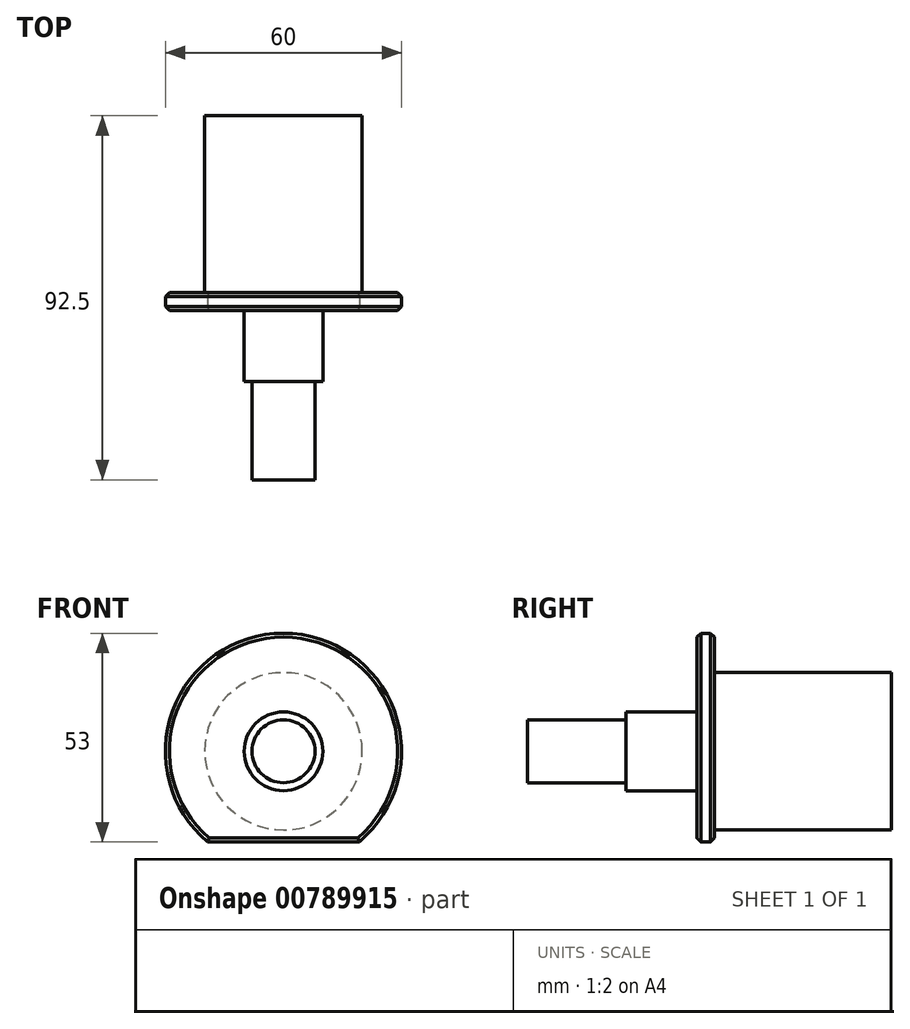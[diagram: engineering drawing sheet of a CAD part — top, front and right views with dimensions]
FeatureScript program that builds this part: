
annotation { "Feature Type Name" : "Feature", "Feature Type Description" : "" }
export const myFeature = defineFeature(function(context is Context, id is Id, definition is map)
    precondition{}
    {
        {
            var Q0;
            Q0=qCreatedBy(makeId("Right.planeOp"),FACE);
            var sketch = newSketch(context, id + "F0", { "sketchPlane" : qUnion([Q0])});
            skLineSegment(sketch, "E0", {"start": v(0, 0) * mm, "end": v(0, -8) * mm});
            skLineSegment(sketch, "E1", {"start": v(0, -8) * mm, "end": v(25, -8) * mm});
            skLineSegment(sketch, "E2", {"start": v(25, -8) * mm, "end": v(25, -10) * mm});
            skLineSegment(sketch, "E3", {"start": v(25, -10) * mm, "end": v(43, -10) * mm});
            skLineSegment(sketch, "E4", {"start": v(43, -10) * mm, "end": v(43, -30) * mm});
            skLineSegment(sketch, "E5", {"start": v(43, -30) * mm, "end": v(47.5, -30) * mm});
            skLineSegment(sketch, "E6", {"start": v(47.5, -30) * mm, "end": v(47.5, -20) * mm});
            skLineSegment(sketch, "E7", {"start": v(47.5, -20) * mm, "end": v(92.5, -20) * mm});
            skLineSegment(sketch, "E8", {"start": v(92.5, -20) * mm, "end": v(92.5, 0) * mm});
            skLineSegment(sketch, "E9", {"start": v(92.5, 0) * mm, "end": v(0, 0) * mm});
            skLineSegment(sketch, "E10", {"start": v(-68.98, 0) * mm, "end": v(144.58, 0) * mm, "construction": true});
            skSolve(sketch);
        }
        {
            var Q0;
            Q0=makeQuery(id+"F0.imprint","IMPRINT",FACE,{"disambiguationData":[TD([[makeQuery(id+"F0.imprint","IMPRINT",EDGE,{"derivedFrom":sQuery(id+"F0.wireOp",EDGE,"E0")}),1.0]])]});
            var Q1;
            Q1=sQuery(id+"F0.wireOp",EDGE,"E10");
            revolve(context, id + "F1", {"surfaceOperationType" : NewSurfaceOperationType.NEW, "entities" : qUnion([Q0]), "axis" : qUnion([Q1]), "revolveType" : RevolveType.FULL});
        }
        {
            var Q0;
            Q0=qCreatedBy(makeId("Front.planeOp"),FACE);
            var sketch = newSketch(context, id + "F2", { "sketchPlane" : qUnion([Q0])});
            skLineSegment(sketch, "E11.bottom", {"start": v(30, -23) * mm, "end": v(-30, -23) * mm});
            skLineSegment(sketch, "E11.top", {"start": v(30, -33) * mm, "end": v(-30, -33) * mm});
            skLineSegment(sketch, "E11.left", {"start": v(30, -23) * mm, "end": v(30, -33) * mm});
            skLineSegment(sketch, "E11.right", {"start": v(-30, -23) * mm, "end": v(-30, -33) * mm});
            skSolve(sketch);
        }
        {
            var Q0;
            Q0=qSketchRegion(id+"F2",true);
            extrude(context, id + "F3", {"entities" : qUnion([Q0]), "operationType" : NewBodyOperationType.REMOVE, "endBound" : BoundingType.THROUGH_ALL, "oppositeDirection" : true, "depth" : 25 * mm, "offsetDistance" : 25 * mm});
        }
        {
            var Q0;
            Q0=makeQuery(id+"F1.opRevolve","SWEPT_EDGE",EDGE,{"disambiguationData":[OSD([sQuery(id+"F0.wireOp",EDGE,"E5"),sQuery(id+"F0.wireOp",EDGE,"E6")])]});
            var Q1;
            Q1=makeQuery(id+"F3.boolean.opBoolean","INTERSECT",EDGE,{"derivedFrom":[makeQuery(id+"F1.opRevolve","SWEPT_FACE",FACE,{"disambiguationData":[OSD([sQuery(id+"F0.wireOp",EDGE,"E6")])]}),makeQuery(id+"F3.opExtrude","SWEPT_FACE",FACE,{"disambiguationData":[OSD([sQuery(id+"F2.wireOp",EDGE,"E11.bottom")])]})]});
            var Q2;
            Q2=makeQuery(id+"F1.opRevolve","SWEPT_EDGE",EDGE,{"disambiguationData":[OSD([sQuery(id+"F0.wireOp",EDGE,"E4"),sQuery(id+"F0.wireOp",EDGE,"E5")])]});
            var Q3;
            Q3=makeQuery(id+"F3.boolean.opBoolean","INTERSECT",EDGE,{"derivedFrom":[makeQuery(id+"F1.opRevolve","SWEPT_FACE",FACE,{"disambiguationData":[OSD([sQuery(id+"F0.wireOp",EDGE,"E4")])]}),makeQuery(id+"F3.opExtrude","SWEPT_FACE",FACE,{"disambiguationData":[OSD([sQuery(id+"F2.wireOp",EDGE,"E11.bottom")])]})]});
            chamfer(context, id + "F4", {"entities" : qUnion([Q0, Q1, Q2, Q3]), "width" : 1 * mm, "tangentPropagation" : true});
        }
    });
